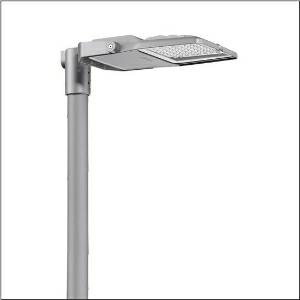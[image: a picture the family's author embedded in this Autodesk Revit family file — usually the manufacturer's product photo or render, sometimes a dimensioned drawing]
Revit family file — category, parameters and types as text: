
# Revit family: floodlight_fl_21_mini___pl52_5xa7776b4d3a_8fbb
name_source: partatom
category: Lighting Fixtures
units: mm (PartAtom-declared; Revit-internal decimal feet)

## family parameters
Cut with Voids When Loaded = No
Host = Face
Light Source = No
Part Type = Normal
Room Calculation Point = No
Round Connector Dimension = Use Diameter
Shared = No

## types (1)
- --- (1 x LED, 6480 lm, 45.7 W, 4000K)
    Apparent Load = 46 VA
    CIE Flux Codes = 26 60 98 100 100
    Color Rendering = 70
    Color Temperature = 4000K
    Default Elevation = 1800 mm
    Description = Floodlight FL 21 mini, floodlight, primary light control with lens, of PMMA, primary optical cover: protective disc, of toughened safety glass, transparent, light distribution: PL52, light emission: direct distribution, installation type: surface-mounted, LED, High Power LED, rated luminous flux: 6.480lm, luminous efficacy: 142lm/W, light colour: 740, colour temperature: 4000K, control gear: D4iSmart Interface (Zhaga), control: overheat protection, constant luminous flux control, time-dependent luminous flux control, flexible luminous flux parameterisation, pre-setting: logarithmic dimming characteristic, with terminal, 6-pole, mains connection: 220..240V, AC, 50/60Hz, start of lifetime: 46W, end of service life: 48W, reduction: 22W, mast bracket, of diecast aluminium, powder-coated, SITECO metallic grey (DB 702S), corrosivity category C5 mid according to DIN EN ISO 12944, suitable for swimming pools, chlorine-resistant, sealing non-destructively replaceable, mast bracket, of steel, galvanised, powder-coated, SITECO metallic grey (DB 702S), Smart Interface below and above, protection rating (complete): IP66, insulation class (complete): insulation class II (safety insulation), certification: CE, ENEC, VDE, protection symbol: D, impact resistance: IK08, permissible operating ambient temperature: -40..+40°C, permissible operating ambient temperature for outdoor applications: -40..+50°C, standard: DIN EN 12944, LABS conformity tested according to VDMA 24364:2018-05, packaging unit: 1 piece

Light Distribution: PL52
    Height = 70 mm
    Lamp = 1 x LED
    Lamp Light Flux = 6480 lm
    Lamp Power = 45.7 W
    Lamp count = 1
    Length = 485 mm
    Luminous efficacy = 142 lm/W
    Manufacturer = Siteco
    ModVariant = No
    Model = 5XA7776B4D3A
    Number of Poles = 1
    OnlyDefault = Yes
    Power Factor = 1
    Product Name = Floodlight FL 21 mini | PL52
    Product group = floodlight | pylon annexe
    ProductGroupID = 6201
    Protection Class = Protection class II
    Protection Degree = IP 66
    RLX_Detail_Level = 1
    RLX_Emergency_Light_Flux = 0 lm
    RLX_Emergency_Type = 0
    RLX_Emergency_Type_DB = No
    RlxData = <blob elided: 101169 chars, md5=cc709c86>
    Socket = socket
    Standby Power = 0 W
    System Light Flux = 6480 lm
    System Power = 46 W
    Type Comments = factory setting: luminous flux: 100 % | dim-lin: 254 | 463 mA
    Type Image = l_1007125.jpg
    URL = http://relux.com
    VarID = @adj_099371
    Voltage = 0 V
    Weight = 0.00 kg
    Width = 337 mm

## geometry (parser evidence)
native form markers: Blend x4, Sweep x11
no freeform markers — native parametric forms only
